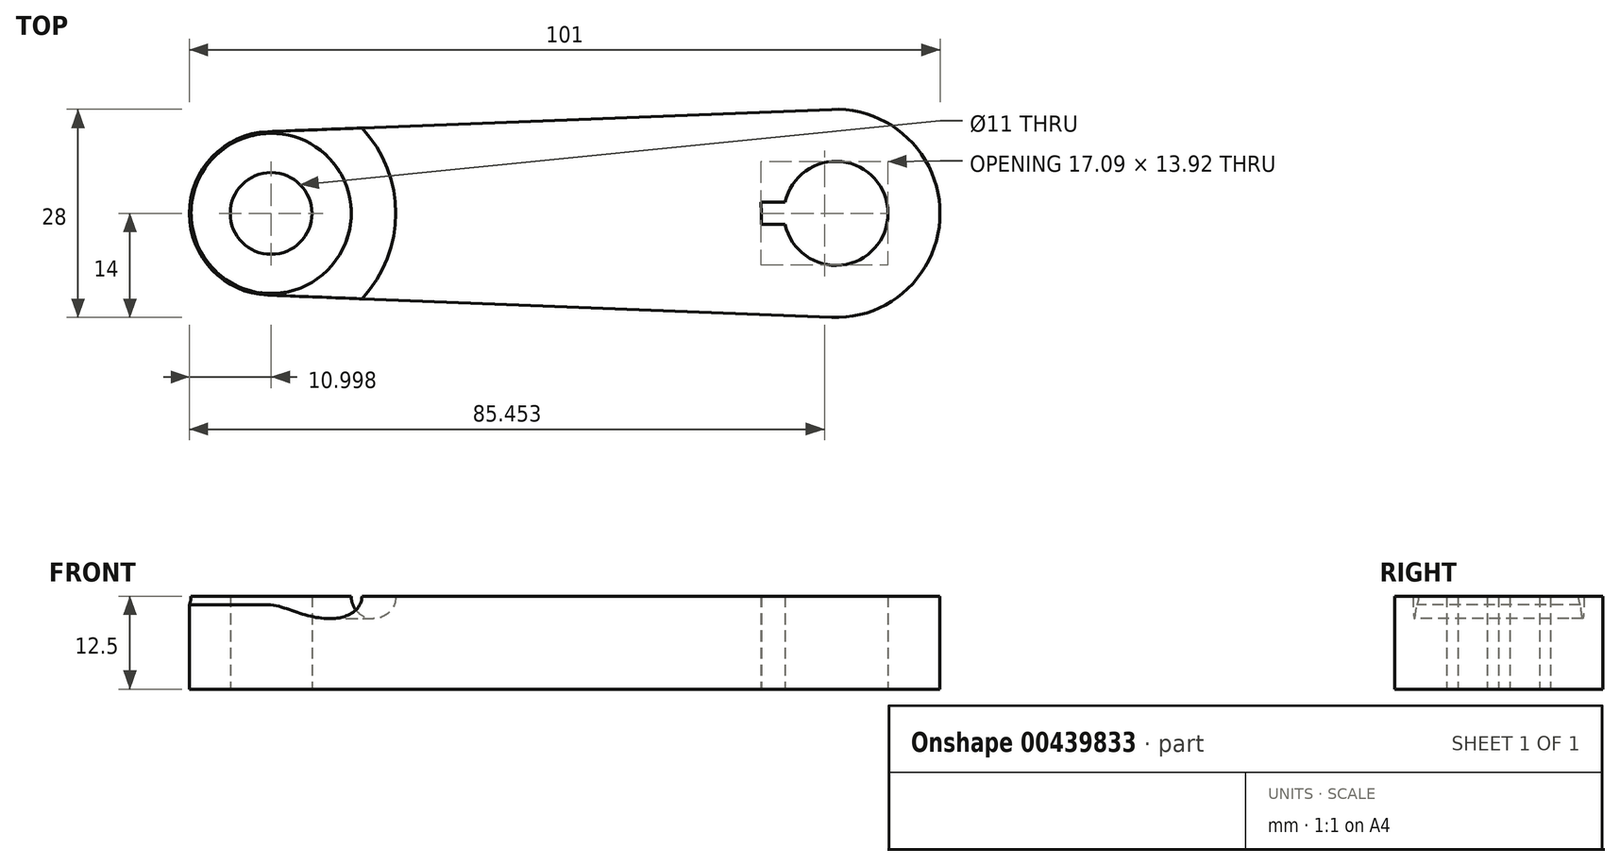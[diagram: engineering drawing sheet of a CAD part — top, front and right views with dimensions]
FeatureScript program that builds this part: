
annotation { "Feature Type Name" : "Feature", "Feature Type Description" : "" }
export const myFeature = defineFeature(function(context is Context, id is Id, definition is map)
    precondition{}
    {
        {
            var Q0;
            Q0=qCreatedBy(makeId("Top.planeOp"),FACE);
            var sketch = newSketch(context, id + "F0", { "sketchPlane" : qUnion([Q0])});
            skCircle(sketch, "E0", {"center": v(-36.74, 0) * mm, "radius": 5.5 * mm});
            skCircle(sketch, "E1", {"center": v(-36.74, 0) * mm, "radius": 11 * mm});
            skArc(sketch, "E2", {"start": v(32.42, -1.5) * mm, "mid": v(46.26, 0) * mm, "end": v(32.42, 1.5) * mm});
            skCircle(sketch, "E3", {"center": v(39.26, 0) * mm, "radius": 14 * mm});
            skLineSegment(sketch, "E4", {"start": v(-37.18, 11) * mm, "end": v(38.7, 13.99) * mm});
            skLineSegment(sketch, "E5", {"start": v(-37.18, -11) * mm, "end": v(38.7, -13.99) * mm});
            skPoint(sketch, "E6", {"position": v(29.23, 0) * mm});
            skLineSegment(sketch, "E7", {"start": v(29.23, 0) * mm, "end": v(29.23, -1.5) * mm});
            skLineSegment(sketch, "E8", {"start": v(29.23, -1.5) * mm, "end": v(32.42, -1.5) * mm});
            skLineSegment(sketch, "E9", {"start": v(29.23, 0) * mm, "end": v(29.17, 1.5) * mm});
            skLineSegment(sketch, "E10", {"start": v(29.17, 1.5) * mm, "end": v(32.42, 1.5) * mm});
            skSolve(sketch);
        }
        {
            var Q0;
            Q0=makeQuery(id+"F0.imprint","IMPRINT",FACE,{"disambiguationData":[TD([[makeQuery(id+"F0.imprint","IMPRINT",EDGE,{"derivedFrom":sQuery(id+"F0.wireOp",EDGE,"E0")}),-1.0]])]});
            var Q1;
            Q1=makeQuery(id+"F0.imprint","IMPRINT",FACE,{"disambiguationData":[TD([[makeQuery(id+"F0.imprint","IMPRINT",EDGE,{"derivedFrom":sQuery(id+"F0.wireOp",EDGE,"E2")}),-1.0]])]});
            var Q2;
            {var subQ0=sQuery(id+"F0.wireOp",EDGE,"E4");Q2=makeQuery(id+"F0.imprint","IMPRINT",FACE,{"disambiguationData":[TD([[makeQuery(id+"F0.imprint","IMPRINT",EDGE,{"derivedFrom":subQ0}),-1.0]])]});}
            extrude(context, id + "F1", {"entities" : qUnion([Q0, Q1, Q2]), "depth" : 12.5 * mm});
        }
        {
            var Q0;
            Q0=qCreatedBy(makeId("Front.planeOp"),FACE);
            var sketch = newSketch(context, id + "F2", { "sketchPlane" : qUnion([Q0])});
            skCircle(sketch, "E11", {"center": v(-50.52, 12.48) * mm, "radius": 3 * mm});
            skSolve(sketch);
        }
        {
            var Q0;
            Q0=makeQuery(id+"F2.imprint","IMPRINT",FACE,{"disambiguationData":[TD([[makeQuery(id+"F2.imprint","IMPRINT",EDGE,{"derivedFrom":sQuery(id+"F2.wireOp",EDGE,"E11")}),1.0]])]});
            var Q1;
            Q1=makeQuery(id+"F1.opExtrude","SWEPT_FACE",FACE,{"disambiguationData":[OSD([sQuery(id+"F0.wireOp",EDGE,"E0")])]});
            revolve(context, id + "F3", {"operationType" : NewBodyOperationType.REMOVE, "entities" : qUnion([Q0]), "axis" : qUnion([Q1]), "revolveType" : RevolveType.FULL, "oppositeDirection" : true});
        }
    });
